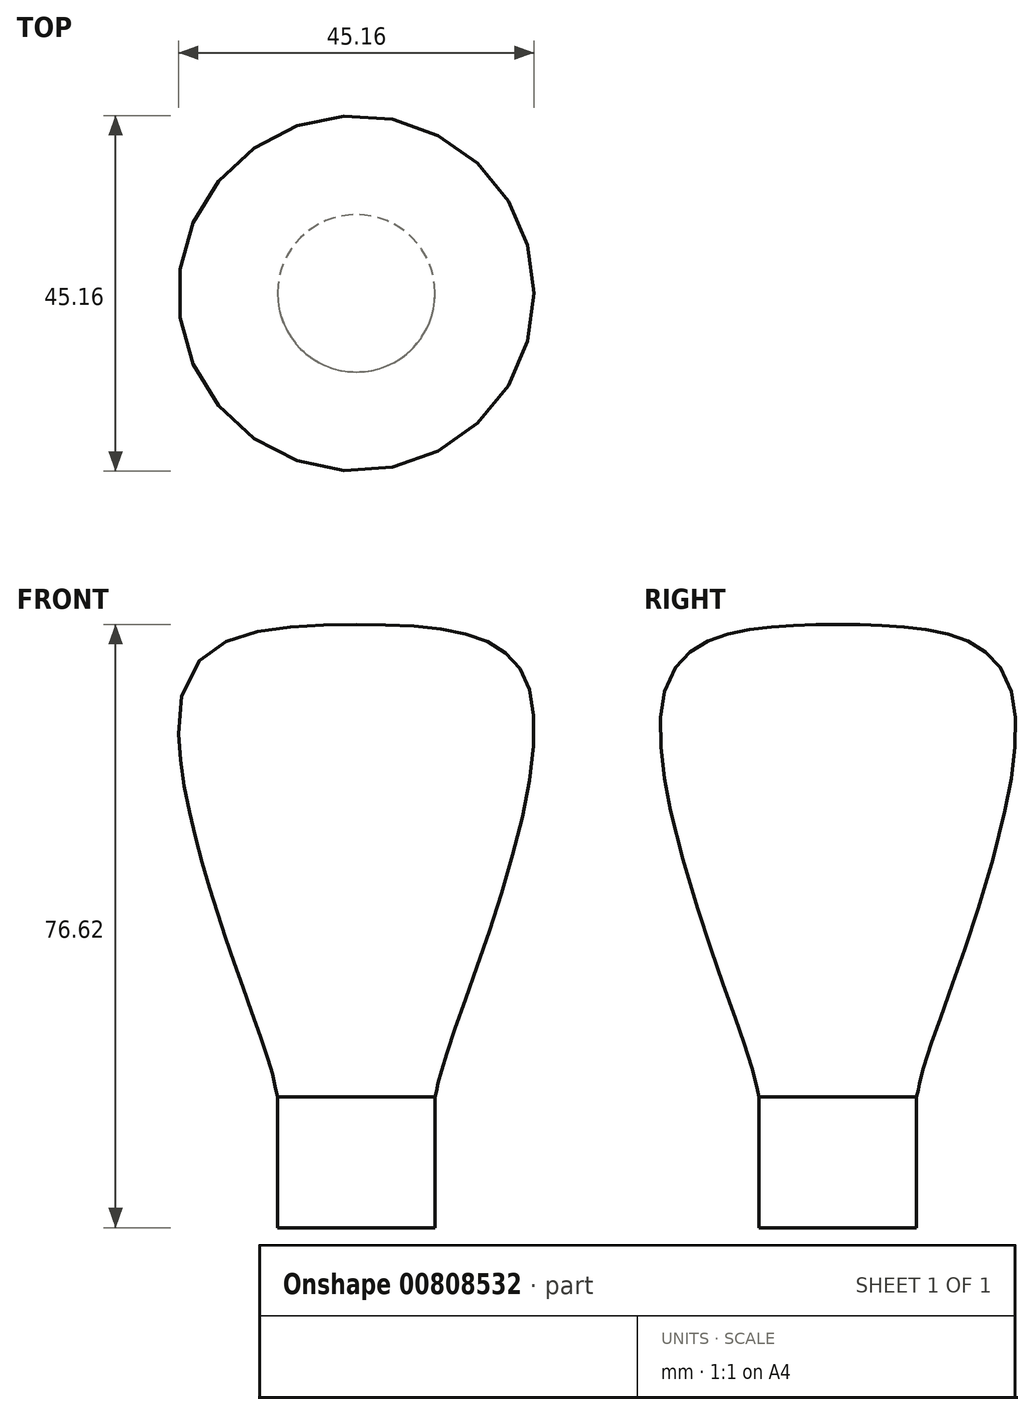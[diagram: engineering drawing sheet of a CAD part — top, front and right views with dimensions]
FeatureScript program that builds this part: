
annotation { "Feature Type Name" : "Feature", "Feature Type Description" : "" }
export const myFeature = defineFeature(function(context is Context, id is Id, definition is map)
    precondition{}
    {
        {
            var Q0;
            Q0=qCreatedBy(makeId("Front.planeOp"),FACE);
            var sketch = newSketch(context, id + "F0", { "sketchPlane" : qUnion([Q0])});
            skLineSegment(sketch, "E0.bottom", {"start": v(-5, 8.31) * mm, "end": v(5, 8.31) * mm});
            skLineSegment(sketch, "E0.top", {"start": v(-5, -8.31) * mm, "end": v(5, -8.31) * mm});
            skLineSegment(sketch, "E0.left", {"start": v(-5, 8.31) * mm, "end": v(-5, -8.31) * mm});
            skLineSegment(sketch, "E0.right", {"start": v(5, 8.31) * mm, "end": v(5, -8.31) * mm});
            skPoint(sketch, "E0.middle", {"position": v(0, 0) * mm});
            skLineSegment(sketch, "E1", {"start": v(-5, 8.31) * mm, "end": v(-5, 68.31) * mm});
            skFitSpline(sketch, "E2", {"points": [v(-5, 68.31) * mm, v(16.96, 60.08) * mm, v(6.08, 12.65) * mm, v(5, 8.31) * mm], "startDerivative": vector(86.5, -0.7) * mm, "endDerivative": vector(-5.34, -14.42) * mm});
            skSolve(sketch);
        }
        {
            var Q0;
            Q0=makeQuery(id+"F0.imprint","IMPRINT",FACE,{"disambiguationData":[TD([[makeQuery(id+"F0.imprint","IMPRINT",EDGE,{"derivedFrom":sQuery(id+"F0.wireOp",EDGE,"E0.bottom")}),1.0]])]});
            var Q1;
            Q1=makeQuery(id+"F0.imprint","IMPRINT",FACE,{"disambiguationData":[TD([[makeQuery(id+"F0.imprint","IMPRINT",EDGE,{"derivedFrom":sQuery(id+"F0.wireOp",EDGE,"E0.bottom")}),-1.0]])]});
            var Q2;
            Q2=sQuery(id+"F0.wireOp",EDGE,"E1");
            revolve(context, id + "F1", {"surfaceOperationType" : NewSurfaceOperationType.NEW, "entities" : qUnion([Q0, Q1]), "axis" : qUnion([Q2]), "revolveType" : RevolveType.FULL});
        }
    });
